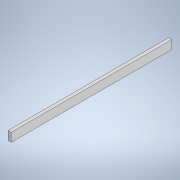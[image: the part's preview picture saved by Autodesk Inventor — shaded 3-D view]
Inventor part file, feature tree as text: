
AUTODESK INVENTOR PART (.ipt)
format: ipt  version: 2021 (Build 250183000, 183)  size: 93,696 bytes
history: native  units: mm
features: other x1, extrude x1, sketch x1
ambient origin geometry x8: Origin, YZ Plane, XZ Plane, XY Plane, X Axis, Y Axis, Z Axis, Center Point
bodies: Body1 (feature_tree)
feature tree (3):
  other  "Твердое тело1"
  extrude  "Выдавливание1"  Depth=1000.0mm
  sketch  "Эскиз1"
